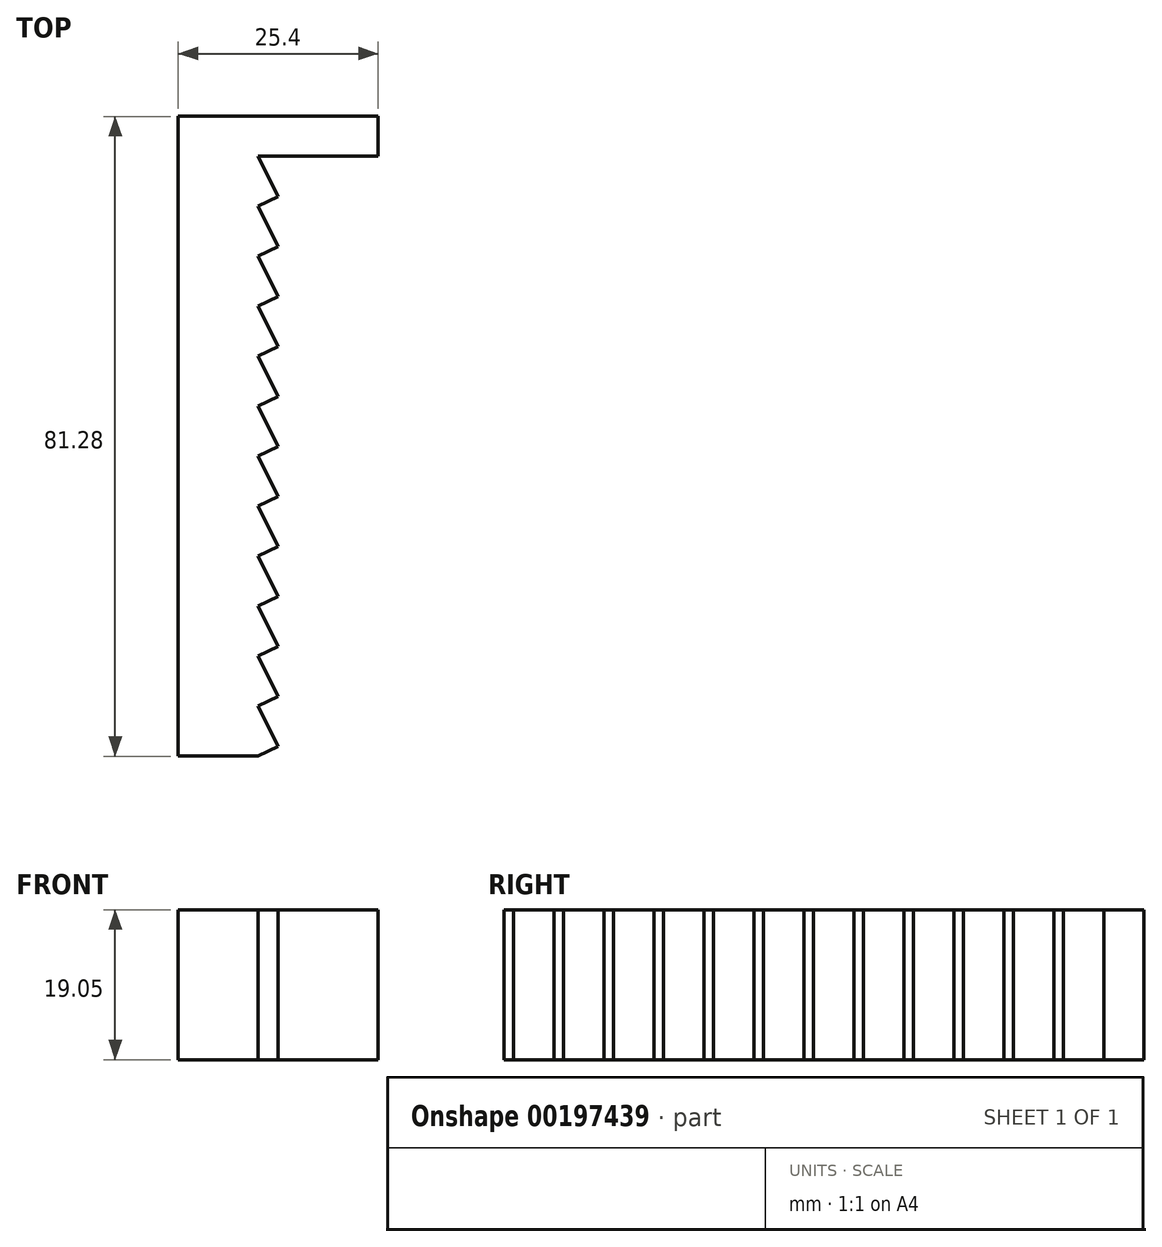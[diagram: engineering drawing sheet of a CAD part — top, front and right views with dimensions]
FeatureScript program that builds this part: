
annotation { "Feature Type Name" : "Feature", "Feature Type Description" : "" }
export const myFeature = defineFeature(function(context is Context, id is Id, definition is map)
    precondition{}
    {
        {
            var Q0;
            Q0=qCreatedBy(makeId("Top.planeOp"),FACE);
            var sketch = newSketch(context, id + "F0", { "sketchPlane" : qUnion([Q0])});
            skLineSegment(sketch, "E0.top", {"start": v(-2.86, -46.2) * mm, "end": v(7.3, -46.2) * mm});
            skLineSegment(sketch, "E0.left", {"start": v(-2.86, 30) * mm, "end": v(-2.86, -46.2) * mm});
            skLineSegment(sketch, "E1", {"start": v(7.3, 30) * mm, "end": v(9.8, 24.86) * mm});
            skLineSegment(sketch, "E2", {"start": v(9.8, 24.86) * mm, "end": v(7.3, 23.65) * mm});
            skLineSegment(sketch, "E3.0.1.0", {"start": v(7.3, 23.65) * mm, "end": v(9.8, 18.51) * mm});
            skLineSegment(sketch, "E3.0.1.1", {"start": v(9.8, 18.51) * mm, "end": v(7.3, 17.3) * mm});
            skLineSegment(sketch, "E3.0.2.0", {"start": v(7.3, 17.3) * mm, "end": v(9.8, 12.16) * mm});
            skLineSegment(sketch, "E3.0.2.1", {"start": v(9.8, 12.16) * mm, "end": v(7.3, 10.95) * mm});
            skLineSegment(sketch, "E3.0.3.0", {"start": v(7.3, 10.95) * mm, "end": v(9.8, 5.81) * mm});
            skLineSegment(sketch, "E3.0.3.1", {"start": v(9.8, 5.81) * mm, "end": v(7.3, 4.6) * mm});
            skLineSegment(sketch, "E3.0.4.0", {"start": v(7.3, 4.6) * mm, "end": v(9.8, -0.54) * mm});
            skLineSegment(sketch, "E3.0.4.1", {"start": v(9.8, -0.54) * mm, "end": v(7.3, -1.75) * mm});
            skLineSegment(sketch, "E3.0.5.0", {"start": v(7.3, -1.75) * mm, "end": v(9.8, -6.89) * mm});
            skLineSegment(sketch, "E3.0.5.1", {"start": v(9.8, -6.89) * mm, "end": v(7.3, -8.1) * mm});
            skLineSegment(sketch, "E3.direction2", {"start": v(9.8, 24.86) * mm, "end": v(9.8, 18.51) * mm, "construction": true});
            skLineSegment(sketch, "E4.0.0.6", {"start": v(7.3, -8.1) * mm, "end": v(9.8, -13.24) * mm});
            skLineSegment(sketch, "E4.3.0.6", {"start": v(9.8, -13.24) * mm, "end": v(7.3, -14.45) * mm});
            skLineSegment(sketch, "E4.0.0.7", {"start": v(7.3, -14.45) * mm, "end": v(9.8, -19.59) * mm});
            skLineSegment(sketch, "E4.3.0.7", {"start": v(9.8, -19.59) * mm, "end": v(7.3, -20.8) * mm});
            skLineSegment(sketch, "E4.0.0.8", {"start": v(7.3, -20.8) * mm, "end": v(9.8, -25.94) * mm});
            skLineSegment(sketch, "E4.3.0.8", {"start": v(9.8, -25.94) * mm, "end": v(7.3, -27.15) * mm});
            skLineSegment(sketch, "E4.0.0.9", {"start": v(7.3, -27.15) * mm, "end": v(9.8, -32.29) * mm});
            skLineSegment(sketch, "E4.3.0.9", {"start": v(9.8, -32.29) * mm, "end": v(7.3, -33.5) * mm});
            skLineSegment(sketch, "E4.0.0.10", {"start": v(7.3, -33.5) * mm, "end": v(9.8, -38.64) * mm});
            skLineSegment(sketch, "E4.3.0.10", {"start": v(9.8, -38.64) * mm, "end": v(7.3, -39.85) * mm});
            skLineSegment(sketch, "E4.0.0.11", {"start": v(7.3, -39.85) * mm, "end": v(9.8, -44.99) * mm});
            skLineSegment(sketch, "E4.3.0.11", {"start": v(9.8, -44.99) * mm, "end": v(7.3, -46.2) * mm});
            skLineSegment(sketch, "E5.bottom", {"start": v(7.3, 30) * mm, "end": v(22.54, 30) * mm});
            skLineSegment(sketch, "E5.top", {"start": v(-2.86, 35.08) * mm, "end": v(22.54, 35.08) * mm});
            skLineSegment(sketch, "E5.left", {"start": v(-2.86, 30) * mm, "end": v(-2.86, 35.08) * mm});
            skLineSegment(sketch, "E5.right", {"start": v(22.54, 30) * mm, "end": v(22.54, 35.08) * mm});
            skLineSegment(sketch, "E6.left", {"start": v(-2.86, 35.08) * mm, "end": v(-2.86, -46.2) * mm});
            skSolve(sketch);
        }
        {
            var Q0;
            Q0 = qSketchRegion(id + "F0", true);
            extrude(context, id + "F1", {"entities" : qUnion([Q0]), "depth" : 19.05 * mm});
        }
    });
